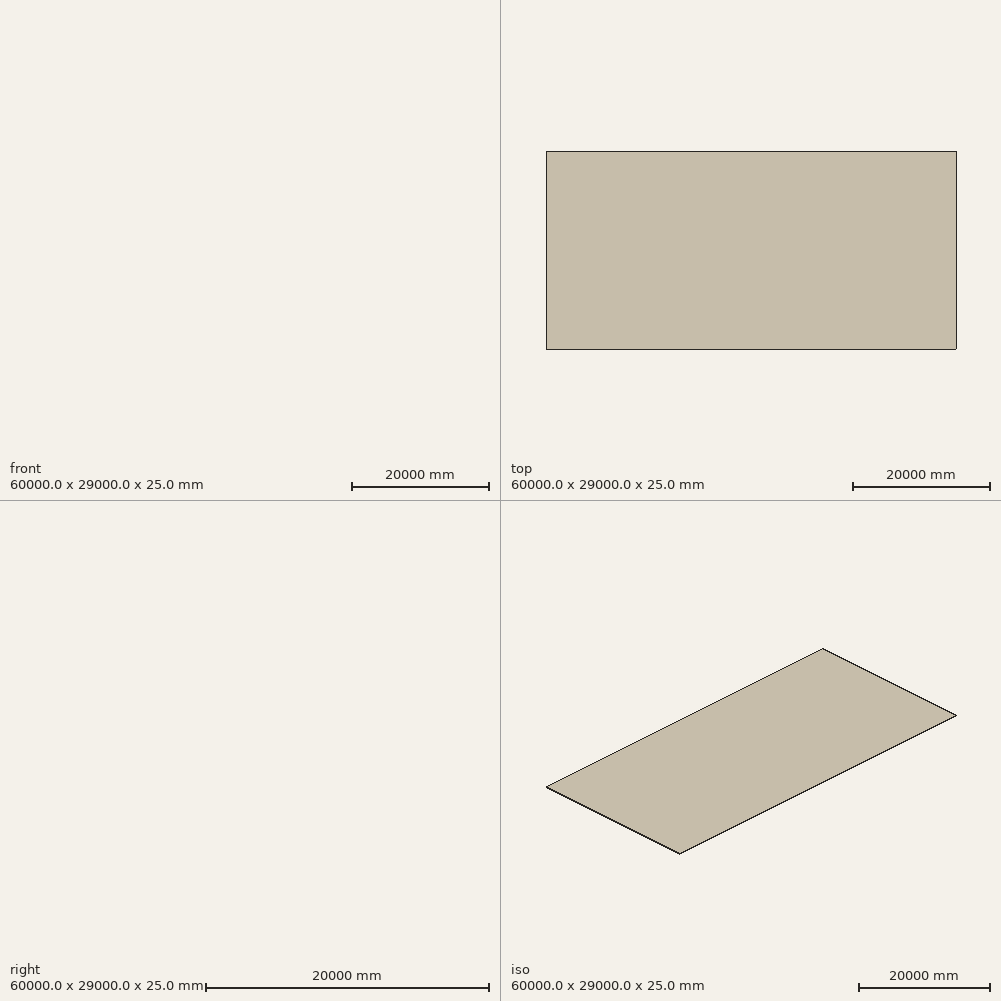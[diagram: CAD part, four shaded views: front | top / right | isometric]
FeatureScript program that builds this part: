
annotation { "Feature Type Name" : "Feature", "Feature Type Description" : "" }
export const myFeature = defineFeature(function(context is Context, id is Id, definition is map)
    precondition{}
    {
        {
            var Q0;
            Q0=qCreatedBy(makeId("Top.planeOp"),FACE);
            var sketch = newSketch(context, id + "F0", { "sketchPlane" : qUnion([Q0])});
            skLineSegment(sketch, "E0.bottom", {"start": v(30000, -14500) * mm, "end": v(-30000, -14500) * mm});
            skLineSegment(sketch, "E0.top", {"start": v(30000, 14500) * mm, "end": v(-30000, 14500) * mm});
            skLineSegment(sketch, "E0.left", {"start": v(30000, -14500) * mm, "end": v(30000, 14500) * mm});
            skLineSegment(sketch, "E0.right", {"start": v(-30000, -14500) * mm, "end": v(-30000, 14500) * mm});
            skPoint(sketch, "E0.middle", {"position": v(0, 0) * mm});
            skSolve(sketch);
        }
        {
            var Q0;
            Q0=makeQuery(id+"F0.imprint","IMPRINT",FACE,{"disambiguationData":[TD([[makeQuery(id+"F0.imprint","IMPRINT",EDGE,{"derivedFrom":sQuery(id+"F0.wireOp",EDGE,"E0.bottom")}),-1.0]])]});
            extrude(context, id + "F1", {"entities" : qUnion([Q0]), "depth" : 25 * mm});
        }
    });
